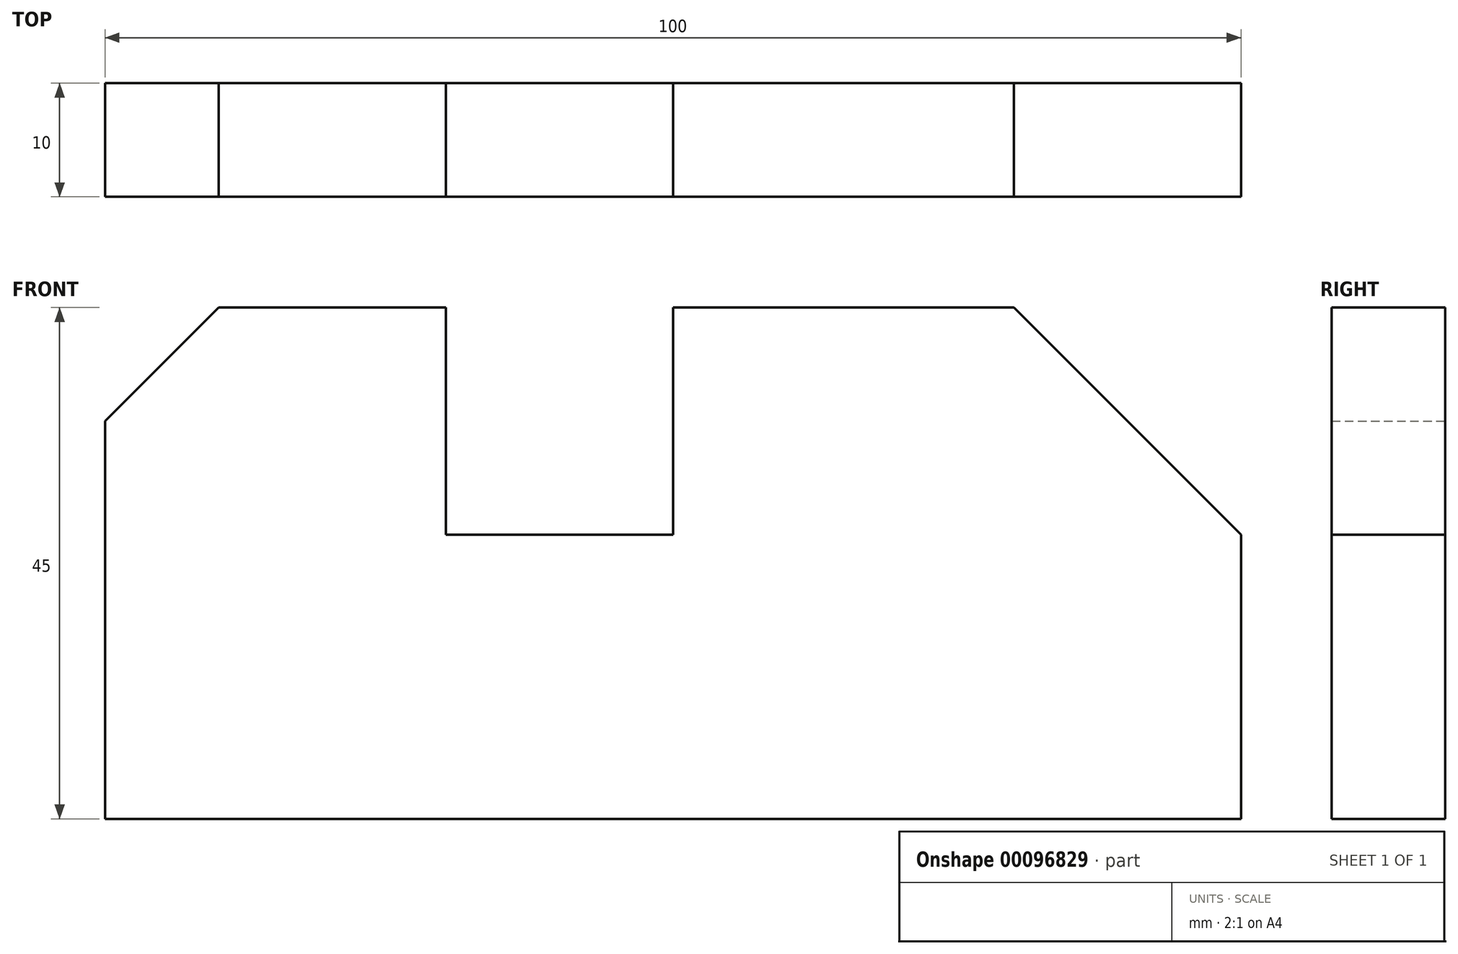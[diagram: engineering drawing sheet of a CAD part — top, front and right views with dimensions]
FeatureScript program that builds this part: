
annotation { "Feature Type Name" : "Feature", "Feature Type Description" : "" }
export const myFeature = defineFeature(function(context is Context, id is Id, definition is map)
    precondition{}
    {
        {
            var Q0;
            Q0=qCreatedBy(makeId("Front.planeOp"),FACE);
            var sketch = newSketch(context, id + "F0", { "sketchPlane" : qUnion([Q0])});
            skLineSegment(sketch, "E0", {"start": v(0, 0) * mm, "end": v(100, 0) * mm});
            skLineSegment(sketch, "E1", {"start": v(100, 0) * mm, "end": v(100, 25) * mm});
            skLineSegment(sketch, "E2", {"start": v(100, 25) * mm, "end": v(80, 45) * mm});
            skLineSegment(sketch, "E3", {"start": v(80, 45) * mm, "end": v(50, 45) * mm});
            skLineSegment(sketch, "E4", {"start": v(50, 45) * mm, "end": v(50, 25) * mm});
            skLineSegment(sketch, "E5", {"start": v(50, 25) * mm, "end": v(30, 25) * mm});
            skLineSegment(sketch, "E6", {"start": v(30, 25) * mm, "end": v(30, 45) * mm});
            skLineSegment(sketch, "E7", {"start": v(0, 0) * mm, "end": v(0, 35) * mm});
            skLineSegment(sketch, "E8", {"start": v(10, 45) * mm, "end": v(30, 45) * mm});
            skLineSegment(sketch, "E9", {"start": v(0, 35) * mm, "end": v(10, 45) * mm});
            skSolve(sketch);
        }
        {
            var Q0;
            Q0 = qSketchRegion(id + "F0", true);
            extrude(context, id + "F1", {"entities" : qUnion([Q0]), "depth" : 10 * mm});
        }
    });
